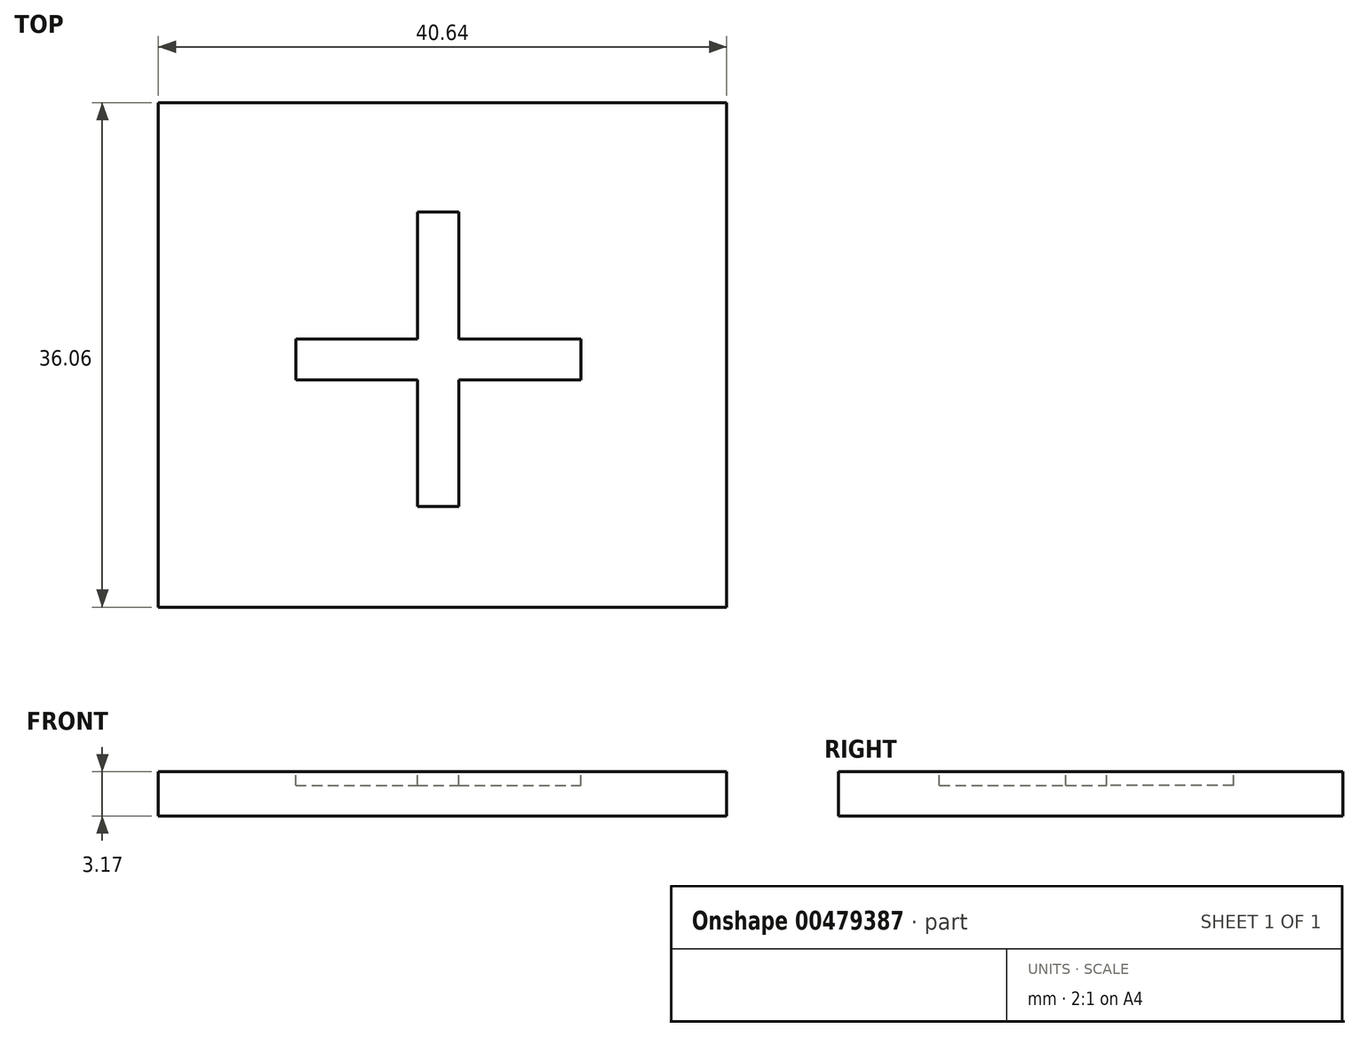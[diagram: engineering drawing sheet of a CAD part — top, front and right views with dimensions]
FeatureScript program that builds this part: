
annotation { "Feature Type Name" : "Feature", "Feature Type Description" : "" }
export const myFeature = defineFeature(function(context is Context, id is Id, definition is map)
    precondition{}
    {
        {
            var Q0;
            Q0=qCreatedBy(makeId("Top.planeOp"),FACE);
            var sketch = newSketch(context, id + "F0", { "sketchPlane" : qUnion([Q0])});
            skLineSegment(sketch, "E0.bottom", {"start": v(-20.32, 18.03) * mm, "end": v(20.32, 18.03) * mm});
            skLineSegment(sketch, "E0.top", {"start": v(-20.32, -18.03) * mm, "end": v(20.32, -18.03) * mm});
            skLineSegment(sketch, "E0.left", {"start": v(-20.32, 18.03) * mm, "end": v(-20.32, -18.03) * mm});
            skLineSegment(sketch, "E0.right", {"start": v(20.32, 18.03) * mm, "end": v(20.32, -18.03) * mm});
            skPoint(sketch, "E0.middle", {"position": v(0, 0) * mm});
            skSolve(sketch);
        }
        {
            var Q0;
            Q0 = qSketchRegion(id + "F0", true);
            extrude(context, id + "F1", {"entities" : qUnion([Q0]), "depth" : 3.17 * mm});
        }
        {
            var Q0;
            Q0=makeQuery(id+"F1.opExtrude","CAP_FACE",FACE,{"disambiguationData":[OSD([sQuery(id+"F0.wireOp",EDGE,"E0.bottom"),sQuery(id+"F0.wireOp",EDGE,"E0.top"),sQuery(id+"F0.wireOp",EDGE,"E0.left"),sQuery(id+"F0.wireOp",EDGE,"E0.right")])],"isStart":false});
            var sketch = newSketch(context, id + "F2", { "sketchPlane" : qUnion([Q0])});
            skText(sketch, "E1", { "text": "+", "fontName": "OpenSans-Regular.ttf"});
            skLineSegment(sketch, "E2", {"start": v(-12.7, 0) * mm, "end": v(0, 15.63) * mm, "construction": true});
            const initialGuessF2  = {"E1": [-0.0127, -0.01563, 1, 0, 0.03127]};
            skSetInitialGuess(sketch, initialGuessF2);
            skSolve(sketch);
        }
        {
            var Q0;
            Q0 = qSketchRegion(id + "F2", true);
            extrude(context, id + "F3", {"entities" : qUnion([Q0]), "operationType" : NewBodyOperationType.REMOVE, "oppositeDirection" : true, "depth" : 1 * mm});
        }
    });
